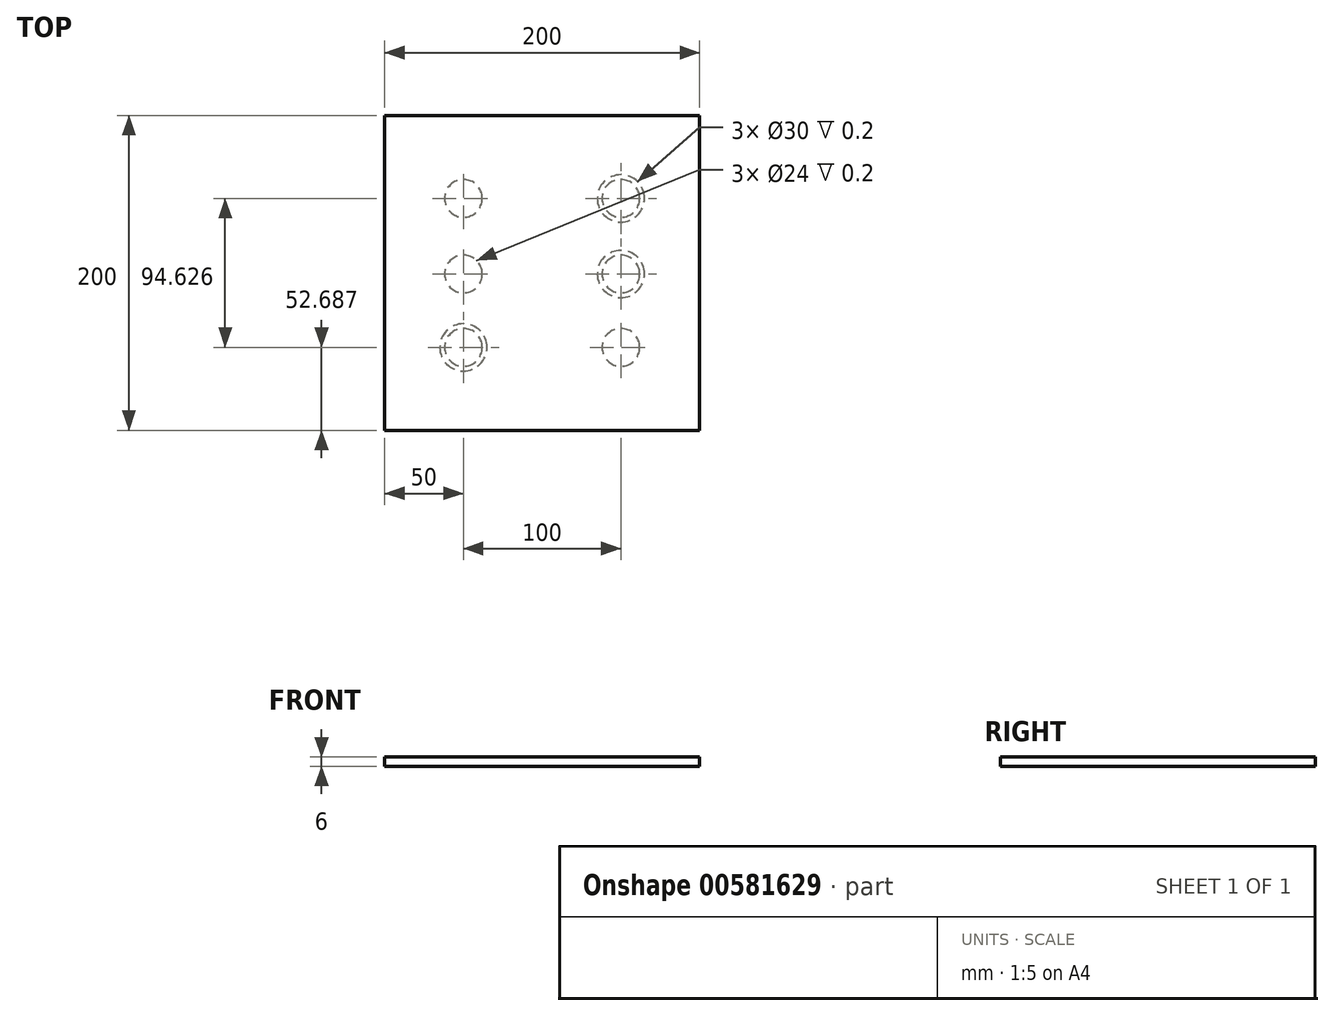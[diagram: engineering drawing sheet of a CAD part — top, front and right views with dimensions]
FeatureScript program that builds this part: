
annotation { "Feature Type Name" : "Feature", "Feature Type Description" : "" }
export const myFeature = defineFeature(function(context is Context, id is Id, definition is map)
    precondition{}
    {
        {
            var Q0;
            Q0=qCreatedBy(makeId("Top.planeOp"),FACE);
            var sketch = newSketch(context, id + "F0", { "sketchPlane" : qUnion([Q0])});
            skLineSegment(sketch, "E0.bottom", {"start": v(100, -100) * mm, "end": v(-100, -100) * mm});
            skLineSegment(sketch, "E0.top", {"start": v(100, 100) * mm, "end": v(-100, 100) * mm});
            skLineSegment(sketch, "E0.left", {"start": v(100, -100) * mm, "end": v(100, 100) * mm});
            skLineSegment(sketch, "E0.right", {"start": v(-100, -100) * mm, "end": v(-100, 100) * mm});
            skPoint(sketch, "E0.middle", {"position": v(0, 0) * mm});
            skSolve(sketch);
        }
        {
            var Q0;
            Q0 = qSketchRegion(id + "F0", true);
            extrude(context, id + "F1", {"entities" : qUnion([Q0]), "endBound" : BoundingType.SYMMETRIC, "depth" : 6 * mm, "offsetDistance" : 25 * mm});
        }
        {
            var Q0;
            Q0=makeQuery(id+"F1.opExtrude","CAP_FACE",FACE,{"disambiguationData":[OSD([sQuery(id+"F0.wireOp",EDGE,"E0.bottom"),sQuery(id+"F0.wireOp",EDGE,"E0.top"),sQuery(id+"F0.wireOp",EDGE,"E0.left"),sQuery(id+"F0.wireOp",EDGE,"E0.right")])],"isStart":true});
            var sketch = newSketch(context, id + "F2", { "sketchPlane" : qUnion([Q0])});
            skCircle(sketch, "E1", {"center": v(50, 0.69) * mm, "radius": 12 * mm});
            skCircle(sketch, "E2", {"center": v(50, -47.31) * mm, "radius": 12 * mm});
            skCircle(sketch, "E3.MirrorC", {"center": v(50, 47.31) * mm, "radius": 12 * mm});
            skCircle(sketch, "E4.MirrorC", {"center": v(-50, -47.31) * mm, "radius": 12 * mm});
            skCircle(sketch, "E5.MirrorC", {"center": v(-50, 0.69) * mm, "radius": 12 * mm});
            skCircle(sketch, "E6.MirrorC", {"center": v(-50, 47.31) * mm, "radius": 12 * mm});
            skCircle(sketch, "E7", {"center": v(50, 0.69) * mm, "radius": 15 * mm});
            skCircle(sketch, "E8", {"center": v(50, -47.31) * mm, "radius": 15 * mm});
            skCircle(sketch, "E9.MirrorC", {"center": v(50, 47.31) * mm, "radius": 15 * mm});
            skCircle(sketch, "E10.MirrorC", {"center": v(-50, -47.31) * mm, "radius": 15 * mm});
            skCircle(sketch, "E11.MirrorC", {"center": v(-50, 0.69) * mm, "radius": 15 * mm});
            skCircle(sketch, "E12.MirrorC", {"center": v(-50, 47.31) * mm, "radius": 15 * mm});
            skSolve(sketch);
        }
        {
            var Q0;
            Q0=makeQuery(id+"F2.imprint","IMPRINT",FACE,{"disambiguationData":[TD([[makeQuery(id+"F2.imprint","IMPRINT",EDGE,{"derivedFrom":sQuery(id+"F2.wireOp",EDGE,"E6.MirrorC")}),-1.0]])]});
            var Q1;
            Q1=makeQuery(id+"F2.imprint","IMPRINT",FACE,{"disambiguationData":[TD([[makeQuery(id+"F2.imprint","IMPRINT",EDGE,{"derivedFrom":sQuery(id+"F2.wireOp",EDGE,"E5.MirrorC")}),1.0]])]});
            var Q2;
            Q2=makeQuery(id+"F2.imprint","IMPRINT",FACE,{"disambiguationData":[TD([[makeQuery(id+"F2.imprint","IMPRINT",EDGE,{"derivedFrom":sQuery(id+"F2.wireOp",EDGE,"E4.MirrorC")}),1.0]])]});
            var Q3;
            Q3=makeQuery(id+"F2.imprint","IMPRINT",FACE,{"disambiguationData":[TD([[makeQuery(id+"F2.imprint","IMPRINT",EDGE,{"derivedFrom":sQuery(id+"F2.wireOp",EDGE,"E3.MirrorC")}),1.0]])]});
            var Q4;
            Q4=makeQuery(id+"F2.imprint","IMPRINT",FACE,{"disambiguationData":[TD([[makeQuery(id+"F2.imprint","IMPRINT",EDGE,{"derivedFrom":sQuery(id+"F2.wireOp",EDGE,"E1")}),-1.0]])]});
            var Q5;
            Q5=makeQuery(id+"F2.imprint","IMPRINT",FACE,{"disambiguationData":[TD([[makeQuery(id+"F2.imprint","IMPRINT",EDGE,{"derivedFrom":sQuery(id+"F2.wireOp",EDGE,"E2")}),-1.0]])]});
            extrude(context, id + "F3", {"entities" : qUnion([Q0, Q1, Q2, Q3, Q4, Q5]), "operationType" : NewBodyOperationType.REMOVE, "oppositeDirection" : true, "depth" : 0.2 * mm, "offsetDistance" : 25 * mm});
        }
    });
